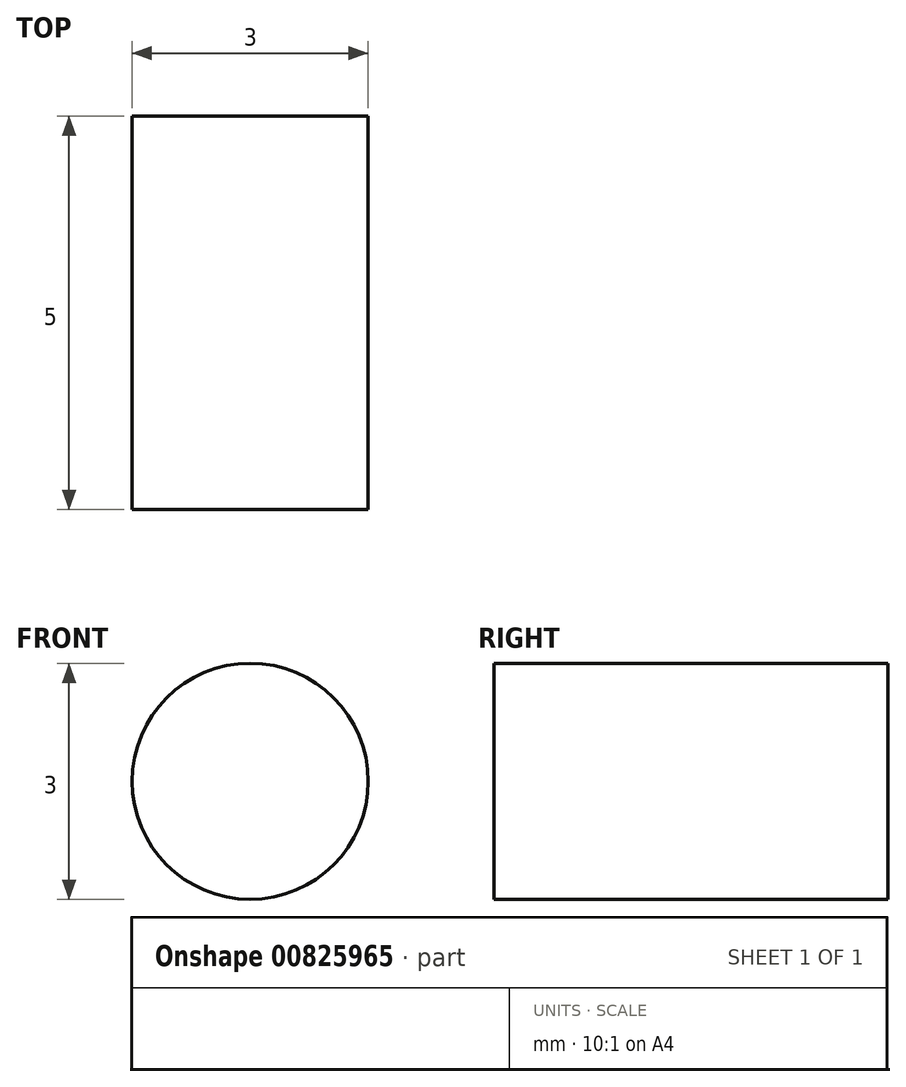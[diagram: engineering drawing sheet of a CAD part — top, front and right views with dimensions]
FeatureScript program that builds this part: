
annotation { "Feature Type Name" : "Feature", "Feature Type Description" : "" }
export const myFeature = defineFeature(function(context is Context, id is Id, definition is map)
    precondition{}
    {
        {
            var Q0;
            Q0=qCreatedBy(makeId("Front.planeOp"),FACE);
            var sketch = newSketch(context, id + "F0", { "sketchPlane" : qUnion([Q0])});
            skCircle(sketch, "E0", {"center": v(0, 0) * mm, "radius": 1.5 * mm});
            skSolve(sketch);
        }
        {
            var Q0;
            Q0 = qSketchRegion(id + "F0", true);
            extrude(context, id + "F1", {"entities" : qUnion([Q0]), "depth" : 5 * mm, "offsetDistance" : 25 * mm});
        }
    });
